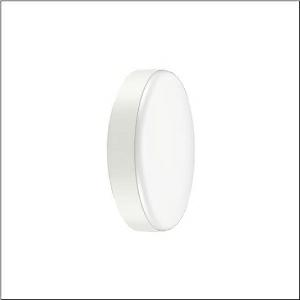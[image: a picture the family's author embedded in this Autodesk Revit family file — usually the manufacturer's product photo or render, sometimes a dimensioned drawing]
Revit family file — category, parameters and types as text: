
# Revit family: round_31_51wc10db34as
name_source: partatom
category: Lighting Fixtures
units: mm (PartAtom-declared; Revit-internal decimal feet)

## family parameters
Cut with Voids When Loaded = No
Host = Face
Light Source = No
Part Type = Normal
Room Calculation Point = No
Round Connector Dimension = Use Diameter
Shared = No

## types (1)
- Round 31 (1 x LED, 4250 lm, 35.4 W, 3000K)
    Apparent Load = 35 VA
    CIE Flux Codes = 44 75 94 94 100
    Color Rendering = 80
    Color Temperature = 3000K
    Default Elevation = 1800 mm
    Description = Round 31, wall and ceiling luminaire, primary optical cover: cover, of PC, opal, light emission: direct distribution, primary light characteristic: symmetric, installation type: surface-mounted, LED, rated luminous flux: 4.250lm, luminous efficacy: 120lm/W, light colour: 830, colour temperature: 3000K, control gear: DALI 2, with terminal, 5-pole, max. 2.5mm², mains connection: 220..240V, AC, 50/60Hz, rated input power: 35.5W, luminaire housing, of PC, traffic white (RAL 9016), diameter: 480mm, brightness and presence sensor, HF sensor, protection rating (complete): IP65, insulation class (complete): insulation class II (safety insulation), certification: CE, impact resistance: IK10, permissible operating ambient temperature: -20..+40°C, permissible storage temperature: -20..+60°C, packaging unit: 1 piece
    Height = 97 mm
    Lamp = 1 x LED
    Lamp Light Flux = 4250 lm
    Lamp Power = 35.4 W
    Lamp count = 1
    Length = 480 mm
    Luminous efficacy = 120 lm/W
    Manufacturer = Siteco
    ModVariant = No
    Model = 51WC10DB34AS
    Mounting Place = Wall
    Mounting Type = Surface mounted
    Number of Poles = 1
    OnlyDefault = Yes
    Power Factor = 1
    Product Name = Round 31
    Product group = wall and ceiling luminaire | wall mounted
    ProductGroupID = 2001
    Protection Class = Protection class II
    Protection Degree = IP 65
    RLX_Detail_Level = 1
    RLX_Emergency_Light_Flux = 0 lm
    RLX_Emergency_Type = 0
    RLX_Emergency_Type_DB = No
    RlxData = <blob elided: 40937 chars, md5=feef5f98>
    Socket = socket
    Standby Power = 0 W
    System Light Flux = 4250 lm
    System Power = 35 W
    Type Comments = Product without accessories
    Type Image = l_1007188.jpg
    URL = http://relux.com
    VarID = ---
    Voltage = 0 V
    Weight = 0.00 kg
    Width = 0 mm  [stored 0 ft]

note: [stored X ft] marks values corroborated as IEEE doubles in the binary element streams (Revit-internal decimal feet)

## geometry (parser evidence)
native form markers: Blend x4, Sweep x14
no freeform markers — native parametric forms only
